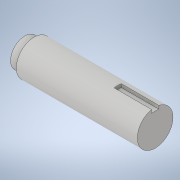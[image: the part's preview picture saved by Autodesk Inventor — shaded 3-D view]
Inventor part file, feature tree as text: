
AUTODESK INVENTOR PART (.ipt)
format: ipt  version: 2021 (Build 250183000, 183)  size: 116,224 bytes
history: native  units: in
note: dims shown in document units (in); Inventor stores cm internally (conversion verified against a paired STEP export)
features: extrude x3, sketch x3, plane x1
ambient origin geometry x8: Origin, YZ Plane, XZ Plane, XY Plane, X Axis, Y Axis, Z Axis, Center Point
bodies: Solid1 (feature_tree)
feature tree (7):
  extrude  "Extrusion1"  Depth=4.565in TaperAngle=0.0deg
  plane  "Work Plane1"
  extrude  "Extrusion9"  Depth=0.25in
  extrude  "Extrusion10"  Depth=1.313in TaperAngle=0.0deg
  sketch  "Sketch1"  dims[d0=1.25in d1=4.565in d2=0.0in]
  sketch  "Sketch9"  dims[d11=-2.0535in d26=0.25in]
  sketch  "Sketch10"  dims[d27=0.125in d28=1.313in d29=0.0in d30=1.0in d31=0.325in d32=0.0in]
